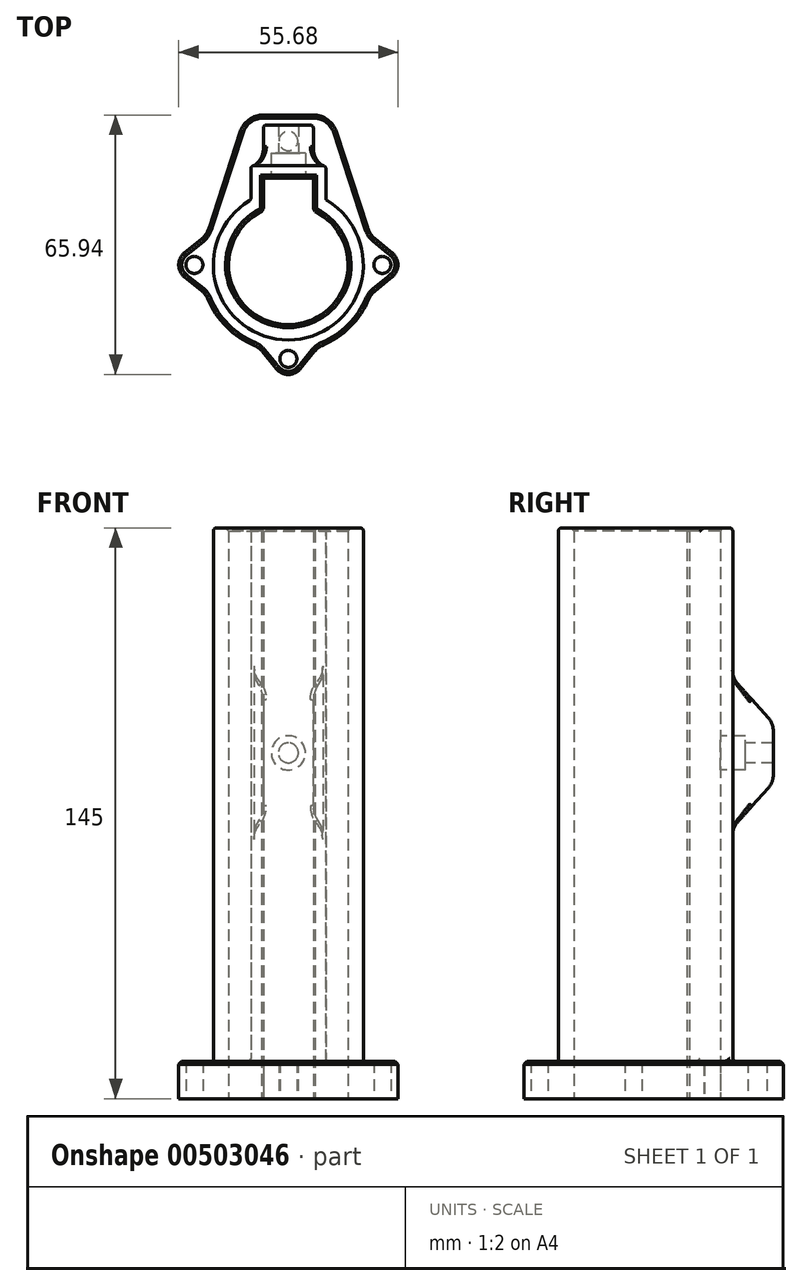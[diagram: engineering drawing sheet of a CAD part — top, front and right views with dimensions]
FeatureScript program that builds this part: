
annotation { "Feature Type Name" : "Feature", "Feature Type Description" : "" }
export const myFeature = defineFeature(function(context is Context, id is Id, definition is map)
    precondition{}
    {
        {
            var Q0;
            Q0=qCreatedBy(makeId("Top.planeOp"),FACE);
            var sketch = newSketch(context, id + "F0", { "sketchPlane" : qUnion([Q0])});
            skArc(sketch, "E0", {"start": v(-6.35, 13.78) * mm, "mid": v(0, -15.18) * mm, "end": v(6.35, 13.78) * mm});
            skArc(sketch, "E1", {"start": v(-9.53, 16.5) * mm, "mid": v(0, -19.05) * mm, "end": v(9.53, 16.5) * mm});
            skLineSegment(sketch, "E2", {"start": v(0, 0) * mm, "end": v(0, 42.76) * mm, "construction": true});
            skLineSegment(sketch, "E3", {"start": v(-6.35, 13.78) * mm, "end": v(-6.35, 22.03) * mm});
            skLineSegment(sketch, "E4", {"start": v(0, -15.18) * mm, "end": v(35.1, -15.18) * mm, "construction": true});
            skLineSegment(sketch, "E5.MirrorCS", {"start": v(6.35, 13.78) * mm, "end": v(6.35, 22.03) * mm});
            skLineSegment(sketch, "E6", {"start": v(6.35, 22.03) * mm, "end": v(-6.35, 22.03) * mm});
            skLineSegment(sketch, "E7", {"start": v(-9.53, 16.5) * mm, "end": v(-9.53, 25.2) * mm});
            skLineSegment(sketch, "E8.MirrorCS", {"start": v(9.53, 16.5) * mm, "end": v(9.53, 25.2) * mm});
            skLineSegment(sketch, "E9", {"start": v(-9.53, 25.2) * mm, "end": v(9.53, 25.2) * mm});
            skSolve(sketch);
        }
        {
            var Q0;
            Q0 = qSketchRegion(id + "F0", true);
            extrude(context, id + "F1", {"entities" : qUnion([Q0]), "depth" : 145 * mm});
        }
        {
            var Q0;
            Q0=qCreatedBy(makeId("Front.planeOp"),FACE);
            cPlane(context, id + "F2", {"entities" : qUnion([Q0]), "cplaneType" : CPlaneType.OFFSET, "offset" : 19.05 * mm, "width" : 152.4 * mm, "height" : 152.4 * mm});
        }
        {
            var Q0;
            Q0=qCreatedBy(makeId("Top.planeOp"),FACE);
            var sketch = newSketch(context, id + "F3", { "sketchPlane" : qUnion([Q0])});
            skArc(sketch, "E10", {"start": v(-6.33, 17.97) * mm, "mid": v(-0.02, -19.05) * mm, "end": v(6.37, 17.95) * mm});
            skLineSegment(sketch, "E11", {"start": v(0, 38.1) * mm, "end": v(-6.25, 38.1) * mm});
            skLineSegment(sketch, "E12", {"start": v(-12.3, 33.7) * mm, "end": v(-20.15, 9.38) * mm});
            skLineSegment(sketch, "E13.MirrorCS", {"start": v(0, 38.1) * mm, "end": v(6.25, 38.1) * mm});
            skLineSegment(sketch, "E14.MirrorCS", {"start": v(12.3, 33.7) * mm, "end": v(20.15, 9.38) * mm});
            skLineSegment(sketch, "E15", {"start": v(-6.33, 17.97) * mm, "end": v(-6.33, 22.04) * mm});
            skLineSegment(sketch, "E16", {"start": v(-6.33, 22.04) * mm, "end": v(6.37, 22.04) * mm});
            skLineSegment(sketch, "E17", {"start": v(6.37, 22.04) * mm, "end": v(6.37, 17.95) * mm});
            skPoint(sketch, "E18.visualSharp", {"position": v(-10.87, 38.1) * mm});
            skArc(sketch, "E18.filletArc", {"start": v(-6.25, 38.1) * mm, "mid": v(-9.99, 36.88) * mm, "end": v(-12.3, 33.7) * mm});
            skPoint(sketch, "E19.visualSharp", {"position": v(10.87, 38.1) * mm});
            skArc(sketch, "E19.filletArc", {"start": v(12.3, 33.7) * mm, "mid": v(9.99, 36.88) * mm, "end": v(6.25, 38.1) * mm});
            skCircle(sketch, "E20", {"center": v(0, 31.45) * mm, "radius": 2.41 * mm});
            skArc(sketch, "E21", {"start": v(-20.15, 9.38) * mm, "mid": v(-20.56, 8.45) * mm, "end": v(-20.92, 7.5) * mm});
            skLineSegment(sketch, "E22", {"start": v(-32.12, 0) * mm, "end": v(31.16, 0) * mm, "construction": true});
            skLineSegment(sketch, "E23", {"start": v(0, 0) * mm, "end": v(0, -26.47) * mm, "construction": true});
            skPoint(sketch, "E23.endSnap0", {"position": v(0, -22.23) * mm});
            skCircle(sketch, "E24", {"center": v(-23.88, 0) * mm, "radius": 2.17 * mm});
            skArc(sketch, "E25", {"start": v(-26, 3.35) * mm, "mid": v(-27.84, 0) * mm, "end": v(-26, -3.35) * mm});
            skLineSegment(sketch, "E26", {"start": v(-26, -3.35) * mm, "end": v(-20.92, -7.5) * mm});
            skLineSegment(sketch, "E27", {"start": v(-26, 3.35) * mm, "end": v(-20.92, 7.5) * mm});
            skLineSegment(sketch, "E28.1.0", {"start": v(-3.35, -26) * mm, "end": v(-7.5, -20.92) * mm});
            skArc(sketch, "E28.1.1", {"start": v(-3.35, -26) * mm, "mid": v(0, -27.84) * mm, "end": v(3.35, -26) * mm});
            skLineSegment(sketch, "E28.1.2", {"start": v(3.35, -26) * mm, "end": v(7.5, -20.92) * mm});
            skCircle(sketch, "E28.1.3", {"center": v(0, -23.88) * mm, "radius": 2.17 * mm});
            skLineSegment(sketch, "E28.2.0", {"start": v(26, -3.35) * mm, "end": v(20.92, -7.5) * mm});
            skArc(sketch, "E28.2.1", {"start": v(26, -3.35) * mm, "mid": v(27.84, 0) * mm, "end": v(26, 3.35) * mm});
            skLineSegment(sketch, "E28.2.2", {"start": v(26, 3.35) * mm, "end": v(20.92, 7.5) * mm});
            skCircle(sketch, "E28.2.3", {"center": v(23.88, 0) * mm, "radius": 2.17 * mm});
            skLineSegment(sketch, "E28.anchor1", {"start": v(0, 0) * mm, "end": v(-26, -3.35) * mm, "construction": true});
            skLineSegment(sketch, "E28.anchor2", {"start": v(0, 0) * mm, "end": v(26, 3.35) * mm, "construction": true});
            skArc(sketch, "E29.trimOffspring", {"start": v(-20.92, -7.5) * mm, "mid": v(-15.72, -15.72) * mm, "end": v(-7.5, -20.92) * mm});
            skArc(sketch, "E30.trimOffspring", {"start": v(7.5, -20.92) * mm, "mid": v(15.72, -15.72) * mm, "end": v(20.92, -7.5) * mm});
            skArc(sketch, "E31.trimOffspring", {"start": v(20.92, 7.5) * mm, "mid": v(20.56, 8.45) * mm, "end": v(20.15, 9.38) * mm});
            skSolve(sketch);
        }
        {
            var Q0;
            Q0 = qSketchRegion(id + "F3", true);
            extrude(context, id + "F4", {"entities" : qUnion([Q0]), "operationType" : NewBodyOperationType.ADD, "depth" : 9.52 * mm});
        }
        {
            var Q0;
            {var subQ0=sQuery(id+"F3.wireOp",EDGE,"E10");Q0=makeQuery(id+"F4.boolean.opBoolean","SPLIT",EDGE,{"disambiguationData":[topologyDisambiguationEdgeConnected([makeQuery(id+"F1.opExtrude","SWEPT_FACE",FACE,{"disambiguationData":[OSD([sQuery(id+"F0.wireOp",EDGE,"E1")])]})])],"derivedFrom":makeQuery(id+"F4.opExtrude","CAP_EDGE",EDGE,{"disambiguationData":[OSD([subQ0])],"isStart":false})});}
            var Q1;
            Q1=makeQuery(id+"F4.opExtrude","CAP_EDGE",EDGE,{"disambiguationData":[OSD([sQuery(id+"F3.wireOp",EDGE,"0fb1ba65-3de0-42f3-b520-cf0c49b8482a.trimOffspring")])],"isStart":false});
            var Q2;
            Q2=makeQuery(id+"F4.boolean.opBoolean","INTERSECT",EDGE,{"derivedFrom":[makeQuery(id+"F1.opExtrude","SWEPT_FACE",FACE,{"disambiguationData":[OSD([sQuery(id+"F0.wireOp",EDGE,"E9")])]}),makeQuery(id+"F4.opExtrude","CAP_FACE",FACE,{"disambiguationData":[OSD([sQuery(id+"F3.wireOp",EDGE,"E10"),sQuery(id+"F3.wireOp",EDGE,"LaoEJ1o9-HxHa-MNEj-rDVl-XYGlTVEM9bCq"),sQuery(id+"F3.wireOp",EDGE,"E11"),sQuery(id+"F3.wireOp",EDGE,"E12"),sQuery(id+"F3.wireOp",EDGE,"E13.MirrorCS"),sQuery(id+"F3.wireOp",EDGE,"E14.MirrorCS"),sQuery(id+"F3.wireOp",EDGE,"E15"),sQuery(id+"F3.wireOp",EDGE,"E16"),sQuery(id+"F3.wireOp",EDGE,"E17"),sQuery(id+"F3.wireOp",EDGE,"E18.filletArc"),sQuery(id+"F3.wireOp",EDGE,"E19.filletArc"),sQuery(id+"F3.wireOp",EDGE,"ANAOrzVF-TJMR-sTcj-WMlL-zBOTR1g8Nq6C"),sQuery(id+"F3.wireOp",EDGE,"k1LmrCzG-qsVe-R1nk-mYpW-xhVotVyL8Vcn"),sQuery(id+"F3.wireOp",EDGE,"4Og8vz2P-hNYc-tukb-owvH-QtE8VaTuDoGS"),sQuery(id+"F3.wireOp",EDGE,"RTvCNsTt-dwNh-nTtE-WWC8-Ns9pGnDZf8Tq"),sQuery(id+"F3.wireOp",EDGE,"2eldP0qC-9rar-uEQ1-tLiH-U3ELiIMfhGJP"),sQuery(id+"F3.wireOp",EDGE,"iK45U5ri-FLyj-Mvuh-Abqq-ICra6Q4eeu1C"),sQuery(id+"F3.wireOp",EDGE,"8b63ff90-d31b-465d-b028-fbe97b359dcc.trimOffspring"),sQuery(id+"F3.wireOp",EDGE,"0fb1ba65-3de0-42f3-b520-cf0c49b8482a.trimOffspring"),sQuery(id+"F3.wireOp",EDGE,"237461f8-ce44-4d60-b5de-c3f2426a158a.trimOffspring"),sQuery(id+"F3.wireOp",EDGE,"E20")])],"isStart":false})]});
            var Q3;
            Q3=makeQuery(id+"F4.boolean.opBoolean","INTERSECT",EDGE,{"derivedFrom":[makeQuery(id+"F1.opExtrude","SWEPT_FACE",FACE,{"disambiguationData":[OSD([sQuery(id+"F0.wireOp",EDGE,"E7")])]}),makeQuery(id+"F4.opExtrude","CAP_FACE",FACE,{"disambiguationData":[OSD([sQuery(id+"F3.wireOp",EDGE,"E10"),sQuery(id+"F3.wireOp",EDGE,"LaoEJ1o9-HxHa-MNEj-rDVl-XYGlTVEM9bCq"),sQuery(id+"F3.wireOp",EDGE,"E11"),sQuery(id+"F3.wireOp",EDGE,"E12"),sQuery(id+"F3.wireOp",EDGE,"E13.MirrorCS"),sQuery(id+"F3.wireOp",EDGE,"E14.MirrorCS"),sQuery(id+"F3.wireOp",EDGE,"E15"),sQuery(id+"F3.wireOp",EDGE,"E16"),sQuery(id+"F3.wireOp",EDGE,"E17"),sQuery(id+"F3.wireOp",EDGE,"E18.filletArc"),sQuery(id+"F3.wireOp",EDGE,"E19.filletArc"),sQuery(id+"F3.wireOp",EDGE,"ANAOrzVF-TJMR-sTcj-WMlL-zBOTR1g8Nq6C"),sQuery(id+"F3.wireOp",EDGE,"k1LmrCzG-qsVe-R1nk-mYpW-xhVotVyL8Vcn"),sQuery(id+"F3.wireOp",EDGE,"4Og8vz2P-hNYc-tukb-owvH-QtE8VaTuDoGS"),sQuery(id+"F3.wireOp",EDGE,"RTvCNsTt-dwNh-nTtE-WWC8-Ns9pGnDZf8Tq"),sQuery(id+"F3.wireOp",EDGE,"2eldP0qC-9rar-uEQ1-tLiH-U3ELiIMfhGJP"),sQuery(id+"F3.wireOp",EDGE,"iK45U5ri-FLyj-Mvuh-Abqq-ICra6Q4eeu1C"),sQuery(id+"F3.wireOp",EDGE,"8b63ff90-d31b-465d-b028-fbe97b359dcc.trimOffspring"),sQuery(id+"F3.wireOp",EDGE,"0fb1ba65-3de0-42f3-b520-cf0c49b8482a.trimOffspring"),sQuery(id+"F3.wireOp",EDGE,"237461f8-ce44-4d60-b5de-c3f2426a158a.trimOffspring"),sQuery(id+"F3.wireOp",EDGE,"E20")])],"isStart":false})]});
            var Q4;
            Q4=makeQuery(id+"F1.opExtrude","SWEPT_EDGE",EDGE,{"disambiguationData":[OSD([sQuery(id+"F0.wireOp",EDGE,"E7"),sQuery(id+"F0.wireOp",EDGE,"E9")])]});
            var Q5;
            Q5=makeQuery(id+"F1.opExtrude","SWEPT_EDGE",EDGE,{"disambiguationData":[OSD([sQuery(id+"F0.wireOp",EDGE,"E1"),sQuery(id+"F0.wireOp",EDGE,"E7")])]});
            var Q6;
            Q6=makeQuery(id+"F1.opExtrude","SWEPT_EDGE",EDGE,{"disambiguationData":[OSD([sQuery(id+"F0.wireOp",EDGE,"E8.MirrorCS"),sQuery(id+"F0.wireOp",EDGE,"E9")])]});
            var Q7;
            Q7=makeQuery(id+"F1.opExtrude","SWEPT_EDGE",EDGE,{"disambiguationData":[OSD([sQuery(id+"F0.wireOp",EDGE,"E1"),sQuery(id+"F0.wireOp",EDGE,"E8.MirrorCS")])]});
            var Q8;
            Q8=makeQuery(id+"F1.opExtrude","CAP_EDGE",EDGE,{"disambiguationData":[OSD([sQuery(id+"F0.wireOp",EDGE,"E1")])],"isStart":false});
            var Q9;
            Q9=makeQuery(id+"F1.opExtrude","CAP_EDGE",EDGE,{"disambiguationData":[OSD([sQuery(id+"F0.wireOp",EDGE,"E9")])],"isStart":false});
            fillet(context, id + "F5", {"entities" : qUnion([Q0, Q1, Q2, Q3, Q4, Q5, Q6, Q7, Q8, Q9]), "radius" : 0.76 * mm, "tangentPropagation" : true, "allowEdgeOverflow" : false});
        }
        {
            var Q0;
            Q0=makeQuery(id+"F4.opExtrude","SWEPT_EDGE",EDGE,{"disambiguationData":[OSD([sQuery(id+"F3.wireOp",EDGE,"E21"),sQuery(id+"F3.wireOp",EDGE,"E27")])]});
            var Q1;
            Q1=makeQuery(id+"F4.opExtrude","SWEPT_EDGE",EDGE,{"disambiguationData":[OSD([sQuery(id+"F3.wireOp",EDGE,"E26"),sQuery(id+"F3.wireOp",EDGE,"E29.trimOffspring")])]});
            var Q2;
            Q2=makeQuery(id+"F4.opExtrude","SWEPT_EDGE",EDGE,{"disambiguationData":[OSD([sQuery(id+"F3.wireOp",EDGE,"E28.1.0"),sQuery(id+"F3.wireOp",EDGE,"E29.trimOffspring")])]});
            var Q3;
            Q3=makeQuery(id+"F4.opExtrude","SWEPT_EDGE",EDGE,{"disambiguationData":[OSD([sQuery(id+"F3.wireOp",EDGE,"E28.1.2"),sQuery(id+"F3.wireOp",EDGE,"E30.trimOffspring")])]});
            var Q4;
            Q4=makeQuery(id+"F4.opExtrude","SWEPT_EDGE",EDGE,{"disambiguationData":[OSD([sQuery(id+"F3.wireOp",EDGE,"E28.2.0"),sQuery(id+"F3.wireOp",EDGE,"E30.trimOffspring")])]});
            var Q5;
            Q5=makeQuery(id+"F4.opExtrude","SWEPT_EDGE",EDGE,{"disambiguationData":[OSD([sQuery(id+"F3.wireOp",EDGE,"E28.2.2"),sQuery(id+"F3.wireOp",EDGE,"E31.trimOffspring")])]});
            fillet(context, id + "F6", {"entities" : qUnion([Q0, Q1, Q2, Q3, Q4, Q5]), "radius" : 5.08 * mm, "tangentPropagation" : true, "allowEdgeOverflow" : false});
        }
        {
            var Q0;
            Q0=makeQuery(id+"F4.opExtrude","SWEPT_EDGE",EDGE,{"disambiguationData":[OSD([sQuery(id+"F3.wireOp",EDGE,"E12"),sQuery(id+"F3.wireOp",EDGE,"E21")])]});
            var Q1;
            Q1=makeQuery(id+"F4.opExtrude","SWEPT_EDGE",EDGE,{"disambiguationData":[OSD([sQuery(id+"F3.wireOp",EDGE,"E14.MirrorCS"),sQuery(id+"F3.wireOp",EDGE,"E31.trimOffspring")])]});
            var Q2;
            Q2=makeQuery(id+"F4.opExtrude","SWEPT_EDGE",EDGE,{"disambiguationData":[OSD([sQuery(id+"F3.wireOp",EDGE,"E25"),sQuery(id+"F3.wireOp",EDGE,"E27")])]});
            var Q3;
            Q3=makeQuery(id+"F4.opExtrude","SWEPT_EDGE",EDGE,{"disambiguationData":[OSD([sQuery(id+"F3.wireOp",EDGE,"E28.2.1"),sQuery(id+"F3.wireOp",EDGE,"E28.2.2")])]});
            var Q4;
            Q4=makeQuery(id+"F4.opExtrude","SWEPT_EDGE",EDGE,{"disambiguationData":[OSD([sQuery(id+"F3.wireOp",EDGE,"E28.2.0"),sQuery(id+"F3.wireOp",EDGE,"E28.2.1")])]});
            var Q5;
            Q5=makeQuery(id+"F4.opExtrude","SWEPT_EDGE",EDGE,{"disambiguationData":[OSD([sQuery(id+"F3.wireOp",EDGE,"E28.1.1"),sQuery(id+"F3.wireOp",EDGE,"E28.1.2")])]});
            var Q6;
            Q6=makeQuery(id+"F4.opExtrude","SWEPT_EDGE",EDGE,{"disambiguationData":[OSD([sQuery(id+"F3.wireOp",EDGE,"E28.1.0"),sQuery(id+"F3.wireOp",EDGE,"E28.1.1")])]});
            var Q7;
            Q7=makeQuery(id+"F4.opExtrude","SWEPT_EDGE",EDGE,{"disambiguationData":[OSD([sQuery(id+"F3.wireOp",EDGE,"E25"),sQuery(id+"F3.wireOp",EDGE,"E26")])]});
            fillet(context, id + "F7", {"entities" : qUnion([Q0, Q1, Q2, Q3, Q4, Q5, Q6, Q7]), "radius" : 5.08 * mm, "tangentPropagation" : true, "allowEdgeOverflow" : false});
        }
        {
            var Q0;
            Q0=makeQuery(id+"F4.opExtrude","CAP_EDGE",EDGE,{"disambiguationData":[OSD([sQuery(id+"F3.wireOp",EDGE,"E12")])],"isStart":false});
            var Q1;
            Q1=makeQuery(id+"F1.opExtrude","SWEPT_EDGE",EDGE,{"disambiguationData":[OSD([sQuery(id+"F0.wireOp",EDGE,"E0"),sQuery(id+"F0.wireOp",EDGE,"E3")])]});
            var Q2;
            Q2=makeQuery(id+"F1.opExtrude","SWEPT_EDGE",EDGE,{"disambiguationData":[OSD([sQuery(id+"F0.wireOp",EDGE,"E0"),sQuery(id+"F0.wireOp",EDGE,"E5.MirrorCS")])]});
            var Q3;
            Q3=makeQuery(id+"F1.opExtrude","CAP_EDGE",EDGE,{"disambiguationData":[OSD([sQuery(id+"F0.wireOp",EDGE,"E0")])],"isStart":false});
            var Q4;
            Q4=makeQuery(id+"F1.opExtrude","CAP_EDGE",EDGE,{"disambiguationData":[OSD([sQuery(id+"F0.wireOp",EDGE,"E5.MirrorCS")])],"isStart":false});
            var Q5;
            Q5=makeQuery(id+"F1.opExtrude","CAP_EDGE",EDGE,{"disambiguationData":[OSD([sQuery(id+"F0.wireOp",EDGE,"E6")])],"isStart":false});
            var Q6;
            Q6=makeQuery(id+"F1.opExtrude","CAP_EDGE",EDGE,{"disambiguationData":[OSD([sQuery(id+"F0.wireOp",EDGE,"E3")])],"isStart":false});
            chamfer(context, id + "F8", {"entities" : qUnion([Q0, Q1, Q2, Q3, Q4, Q5, Q6]), "width" : 0.76 * mm, "tangentPropagation" : true});
        }
        {
            var Q0;
            Q0=makeQuery(id+"F1.opExtrude","SWEPT_FACE",FACE,{"disambiguationData":[OSD([sQuery(id+"F0.wireOp",EDGE,"E9")])]});
            var sketch = newSketch(context, id + "F9", { "sketchPlane" : qUnion([Q0])});
            skCircle(sketch, "E32", {"center": v(0, 87.85) * mm, "radius": 2.54 * mm});
            skSolve(sketch);
        }
        {
            var Q0;
            Q0 = qSketchRegion(id + "F9", true);
            extrude(context, id + "F10", {"entities" : qUnion([Q0]), "operationType" : NewBodyOperationType.REMOVE, "oppositeDirection" : true, "depth" : 6.35 * mm});
        }
        {
            var Q0;
            Q0=makeQuery(id+"F1.opExtrude","CAP_FACE",FACE,{"disambiguationData":[OSD([sQuery(id+"F0.wireOp",EDGE,"E0"),sQuery(id+"F0.wireOp",EDGE,"E1"),sQuery(id+"F0.wireOp",EDGE,"E3"),sQuery(id+"F0.wireOp",EDGE,"E5.MirrorCS"),sQuery(id+"F0.wireOp",EDGE,"E6"),sQuery(id+"F0.wireOp",EDGE,"E7"),sQuery(id+"F0.wireOp",EDGE,"E8.MirrorCS"),sQuery(id+"F0.wireOp",EDGE,"E9")])],"isStart":false});
            cPlane(context, id + "F11", {"entities" : qUnion([Q0]), "cplaneType" : CPlaneType.OFFSET, "offset" : 0 * mm, "width" : 152.4 * mm, "height" : 152.4 * mm});
        }
        {
            var Q0;
            Q0=qCreatedBy(makeId("Right.planeOp"),FACE);
            var sketch = newSketch(context, id + "F12", { "sketchPlane" : qUnion([Q0])});
            skLineSegment(sketch, "E33", {"start": v(25.2, 87.85) * mm, "end": v(80.03, 87.85) * mm, "construction": true});
            skSolve(sketch);
        }
        {
            var Q0;
            Q0=qCreatedBy(makeId("Right.planeOp"),FACE);
            var sketch = newSketch(context, id + "F13", { "sketchPlane" : qUnion([Q0])});
            skLineSegment(sketch, "E34", {"start": v(25.12, 68.8) * mm, "end": v(35.53, 80.37) * mm});
            skLineSegment(sketch, "E35", {"start": v(25.12, 68.8) * mm, "end": v(25.12, 87.85) * mm});
            skLineSegment(sketch, "E36.MirrorCS", {"start": v(25.12, 106.9) * mm, "end": v(25.12, 87.85) * mm});
            skLineSegment(sketch, "E37.MirrorCS", {"start": v(25.12, 106.9) * mm, "end": v(35.53, 95.33) * mm});
            skLineSegment(sketch, "E38", {"start": v(35.53, 95.33) * mm, "end": v(35.53, 80.37) * mm});
            skSolve(sketch);
        }
        {
            var Q0;
            Q0=makeQuery(id+"F13.imprint","IMPRINT",FACE,{"disambiguationData":[TD([[makeQuery(id+"F13.imprint","IMPRINT",EDGE,{"derivedFrom":sQuery(id+"F13.wireOp",EDGE,"E34")}),1.0]])]});
            extrude(context, id + "F14", {"entities" : qUnion([Q0]), "operationType" : NewBodyOperationType.ADD, "depth" : 6.35 * mm, "hasSecondDirection" : true, "secondDirectionOppositeDirection" : true, "secondDirectionDepth" : 6.35 * mm});
        }
        {
            var Q0;
            Q0=makeQuery(id+"F1.opExtrude","SWEPT_FACE",FACE,{"disambiguationData":[OSD([sQuery(id+"F0.wireOp",EDGE,"E6")])]});
            var sketch = newSketch(context, id + "F15", { "sketchPlane" : qUnion([Q0])});
            skCircle(sketch, "E39", {"center": v(0, 87.85) * mm, "radius": 4.34 * mm});
            skSolve(sketch);
        }
        {
            var Q0;
            Q0 = qSketchRegion(id + "F15", true);
            extrude(context, id + "F16", {"entities" : qUnion([Q0]), "operationType" : NewBodyOperationType.REMOVE, "oppositeDirection" : true, "depth" : 6.35 * mm});
        }
        {
            var Q0;
            Q0=makeQuery(id+"F1.opExtrude","SWEPT_FACE",FACE,{"disambiguationData":[OSD([sQuery(id+"F0.wireOp",EDGE,"E6")])]});
            var sketch = newSketch(context, id + "F17", { "sketchPlane" : qUnion([Q0])});
            skCircle(sketch, "E40", {"center": v(0, 87.85) * mm, "radius": 2.54 * mm});
            skSolve(sketch);
        }
        {
            var Q0;
            Q0 = qSketchRegion(id + "F17", true);
            extrude(context, id + "F18", {"entities" : qUnion([Q0]), "operationType" : NewBodyOperationType.REMOVE, "oppositeDirection" : true, "depth" : 25.4 * mm});
        }
        {
            var Q0;
            Q0=makeQuery(id+"F14.boolean.opBoolean","INTERSECT",EDGE,{"derivedFrom":[makeQuery(id+"F1.opExtrude","SWEPT_FACE",FACE,{"disambiguationData":[OSD([sQuery(id+"F0.wireOp",EDGE,"E9")])]}),makeQuery(id+"F14.opExtrude","SWEPT_FACE",FACE,{"disambiguationData":[OSD([sQuery(id+"F13.wireOp",EDGE,"E34")])]})]});
            var Q1;
            Q1=makeQuery(id+"F14.boolean.opBoolean","INTERSECT",EDGE,{"derivedFrom":[makeQuery(id+"F1.opExtrude","SWEPT_FACE",FACE,{"disambiguationData":[OSD([sQuery(id+"F0.wireOp",EDGE,"E9")])]}),makeQuery(id+"F14.opExtrude","SWEPT_FACE",FACE,{"disambiguationData":[OSD([sQuery(id+"F13.wireOp",EDGE,"E37.MirrorCS")])]})]});
            var Q2;
            Q2=makeQuery(id+"F14.opExtrude","SWEPT_EDGE",EDGE,{"disambiguationData":[OSD([sQuery(id+"F13.wireOp",EDGE,"E37.MirrorCS"),sQuery(id+"F13.wireOp",EDGE,"E38")])]});
            var Q3;
            Q3=makeQuery(id+"F14.opExtrude","SWEPT_EDGE",EDGE,{"disambiguationData":[OSD([sQuery(id+"F13.wireOp",EDGE,"E34"),sQuery(id+"F13.wireOp",EDGE,"E38")])]});
            fillet(context, id + "F19", {"entities" : qUnion([Q0, Q1, Q2, Q3]), "radius" : 5.08 * mm, "tangentPropagation" : true, "allowEdgeOverflow" : false});
        }
        {
            var Q0;
            Q0=makeQuery(id+"F14.boolean.opBoolean","INTERSECT",EDGE,{"derivedFrom":[makeQuery(id+"F1.opExtrude","SWEPT_FACE",FACE,{"disambiguationData":[OSD([sQuery(id+"F0.wireOp",EDGE,"E9")])]}),makeQuery(id+"F14.opExtrude","CAP_FACE",FACE,{"disambiguationData":[OSD([sQuery(id+"F13.wireOp",EDGE,"E34"),sQuery(id+"F13.wireOp",EDGE,"E35"),sQuery(id+"F13.wireOp",EDGE,"E36.MirrorCS"),sQuery(id+"F13.wireOp",EDGE,"E37.MirrorCS"),sQuery(id+"F13.wireOp",EDGE,"E38")])],"isStart":false})]});
            var Q1;
            Q1=makeQuery(id+"F14.boolean.opBoolean","INTERSECT",EDGE,{"derivedFrom":[makeQuery(id+"F1.opExtrude","SWEPT_FACE",FACE,{"disambiguationData":[OSD([sQuery(id+"F0.wireOp",EDGE,"E9")])]}),makeQuery(id+"F14.opExtrude","CAP_FACE",FACE,{"disambiguationData":[OSD([sQuery(id+"F13.wireOp",EDGE,"E34"),sQuery(id+"F13.wireOp",EDGE,"E35"),sQuery(id+"F13.wireOp",EDGE,"E36.MirrorCS"),sQuery(id+"F13.wireOp",EDGE,"E37.MirrorCS"),sQuery(id+"F13.wireOp",EDGE,"E38")])],"isStart":true})]});
            fillet(context, id + "F20", {"entities" : qUnion([Q0, Q1]), "radius" : 5.08 * mm, "tangentPropagation" : true, "allowEdgeOverflow" : false});
        }
        {
            var Q0;
            {var subQ0=sQuery(id+"F13.wireOp",EDGE,"E38");var subQ1=sQuery(id+"F13.wireOp",EDGE,"E37.MirrorCS");Q0=makeQuery(id+"F19.opFillet","BLEND_EDGE",EDGE,{"blendedFrom":[makeQuery(id+"F14.opExtrude","SWEPT_EDGE",EDGE,{"disambiguationData":[OSD([subQ1,subQ0])]}),makeQuery(id+"F14.opExtrude","CAP_FACE",FACE,{"disambiguationData":[OSD([sQuery(id+"F13.wireOp",EDGE,"E34"),sQuery(id+"F13.wireOp",EDGE,"E35"),sQuery(id+"F13.wireOp",EDGE,"E36.MirrorCS"),subQ1,subQ0])],"isStart":true})],"blendedInto":[makeQuery(id+"F14.opExtrude","CAP_FACE",FACE,{"disambiguationData":[OSD([sQuery(id+"F13.wireOp",EDGE,"E34"),sQuery(id+"F13.wireOp",EDGE,"E35"),sQuery(id+"F13.wireOp",EDGE,"E36.MirrorCS"),subQ1,subQ0])],"isStart":true})]});}
            var Q1;
            Q1=makeQuery(id+"F14.opExtrude","CAP_EDGE",EDGE,{"disambiguationData":[OSD([sQuery(id+"F13.wireOp",EDGE,"E38")])],"isStart":false});
            fillet(context, id + "F21", {"entities" : qUnion([Q0, Q1]), "radius" : 0.76 * mm, "tangentPropagation" : true, "allowEdgeOverflow" : false});
        }
    });
